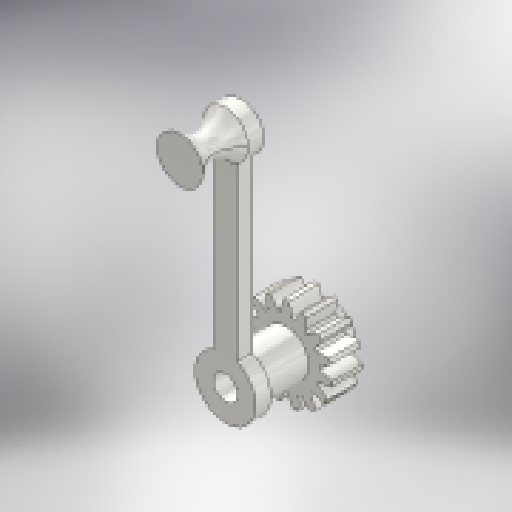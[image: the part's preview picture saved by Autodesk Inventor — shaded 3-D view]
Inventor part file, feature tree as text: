
AUTODESK INVENTOR PART (.ipt)
format: ipt  version: 2024 (Build 280153000, 153)  size: 501,760 bytes
history: native  units: mm (DEFAULTED — no unit token found)
features: plane x6, sketch x6, other x4, extrude x3, hole x1, loft x1
ambient origin geometry x8: Origin, YZ Plane, XZ Plane, XY Plane, X Axis, Y Axis, Z Axis, Center Point
bodies: Solid1 (feature_tree)
feature tree (21):
  extrude  "Extrusion1"  Depth=6.35mm TaperAngle=0.0deg
  plane  "Work Plane1"
  plane  "Work Plane2"
  plane  "Work Plane3"
  other  "Spur Gear"
  extrude  "Extrusion2"  Depth=76.2mm TaperAngle=0.0deg
  sketch  "Sketch4"  dims[d6=0.0mm d7=2.094395mm d9=0.0mm]
  extrude  "Extrusion3"  TaperAngle=0.0deg  [1 undecoded]
  other  "Work Point1"
  hole  "Hole1"  [1 undecoded]
  plane  "Work Plane5"
  sketch  "Sketch7"  dims[d14=0.0mm d15=25.4mm d16=0.0mm]
  sketch  "Sketch8"  dims[d17=0.0mm d18=0.0mm d19=25.4mm d20=101.6mm]
  sketch  "Sketch9"  dims[d21=4.7625mm d22=9.525mm d23=15.875mm d24=0.0mm d25=101.6mm d26=12.7mm d27=9.525mm d29=3.175mm d30=0.0mm d31=4.7625mm d34=9.525mm d35=0.0mm d36=25.4mm d37=25.4mm d38=5.1054mm d39=19.05mm d40=9.525mm d41=6.35mm d42=14.3117mm d43=9.525mm d44=0.0mm d46=4.7625mm d47=4.7625mm d48=4.7625mm d49=0.0mm d50=90.0deg d51=0.0mm d52=90.0deg d53=0.0mm d54=90.0deg]
  loft  "Loft1"
  plane  "Work Plane6"
  sketch  "Sketch1"  dims[d0=19.12mm d1=6.35mm d2=0.0mm]
  other  "Srf1"
  sketch  "Sketch3"  dims[d3=16.875mm d4=76.2mm d5=0.0mm]
  plane  "Work Plane4"
  other  "Pitch Diameter"
note: 2 required parameter values undecoded (feature->parameter linkage not recoverable at this tier; creation-order binding heuristic only, values carry confidence <= 0.55)
